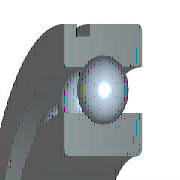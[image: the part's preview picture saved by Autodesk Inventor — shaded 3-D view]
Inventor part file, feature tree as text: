
AUTODESK INVENTOR PART (.ipt)
format: ipt  version: 2015 (Build 190159000, 159)  size: 305,152 bytes
history: native  units: mm (DEFAULTED — no unit token found)
features: sketch x1, other x1, pattern_circular x1
ambient origin geometry x8: Origin, YZ Plane, XZ Plane, XY Plane, X Axis, Y Axis, Z Axis, Center Point
bodies: Solid1 (feature_tree)
feature tree (3):
  sketch  "草图"  dims[d0=4.42mm d17=90.0deg d18=90.0deg d1=0.3mm d2=80.0mm d3=360.0deg d4=0.0mm d5=0.0mm d6=0.0mm d7=15.0mm d8=32.0mm d9=23.5mm d10=30.92mm d11=20.542mm d12=20.542mm d13=20.542mm d14=0.0mm d15=9.0mm d16=9.0mm d19=1.5mm d20=3.0mm d22=4.5mm d23=0.0mm d24=0.0mm]
  other  "轴承体"
  pattern_circular  "IDS_ARRAYBALL[SIMPL:T]"  Angle=90.0deg  [1 undecoded]
note: 1 required parameter value undecoded (feature->parameter linkage not recoverable at this tier; creation-order binding heuristic only, values carry confidence <= 0.55)
